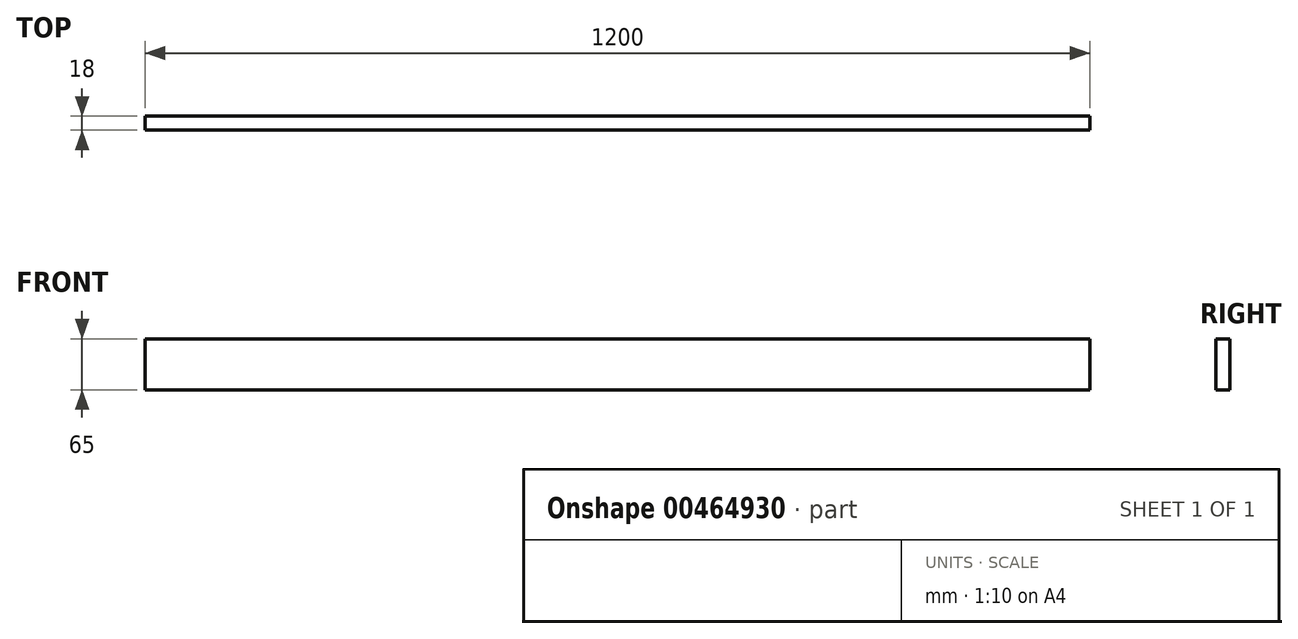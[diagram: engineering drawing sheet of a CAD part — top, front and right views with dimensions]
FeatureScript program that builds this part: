
annotation { "Feature Type Name" : "Feature", "Feature Type Description" : "" }
export const myFeature = defineFeature(function(context is Context, id is Id, definition is map)
    precondition{}
    {
        {
            var Q0;
            Q0=qCreatedBy(makeId("Right.planeOp"),FACE);
            var sketch = newSketch(context, id + "F0", { "sketchPlane" : qUnion([Q0])});
            skLineSegment(sketch, "E0.bottom", {"start": v(-9, 32.5) * mm, "end": v(9, 32.5) * mm});
            skLineSegment(sketch, "E0.top", {"start": v(-9, -32.5) * mm, "end": v(9, -32.5) * mm});
            skLineSegment(sketch, "E0.left", {"start": v(-9, 32.5) * mm, "end": v(-9, -32.5) * mm});
            skLineSegment(sketch, "E0.right", {"start": v(9, 32.5) * mm, "end": v(9, -32.5) * mm});
            skPoint(sketch, "E0.middle", {"position": v(0, 0) * mm});
            skSolve(sketch);
        }
        {
            var Q0;
            Q0=makeQuery(id+"F0.imprint","IMPRINT",FACE,{"disambiguationData":[TD([[makeQuery(id+"F0.imprint","IMPRINT",EDGE,{"derivedFrom":sQuery(id+"F0.wireOp",EDGE,"E0.bottom")}),-1.0]])]});
            extrude(context, id + "F1", {"entities" : qUnion([Q0]), "endBound" : BoundingType.SYMMETRIC, "depth" : 1200 * mm, "offsetDistance" : 25 * mm});
        }
    });
